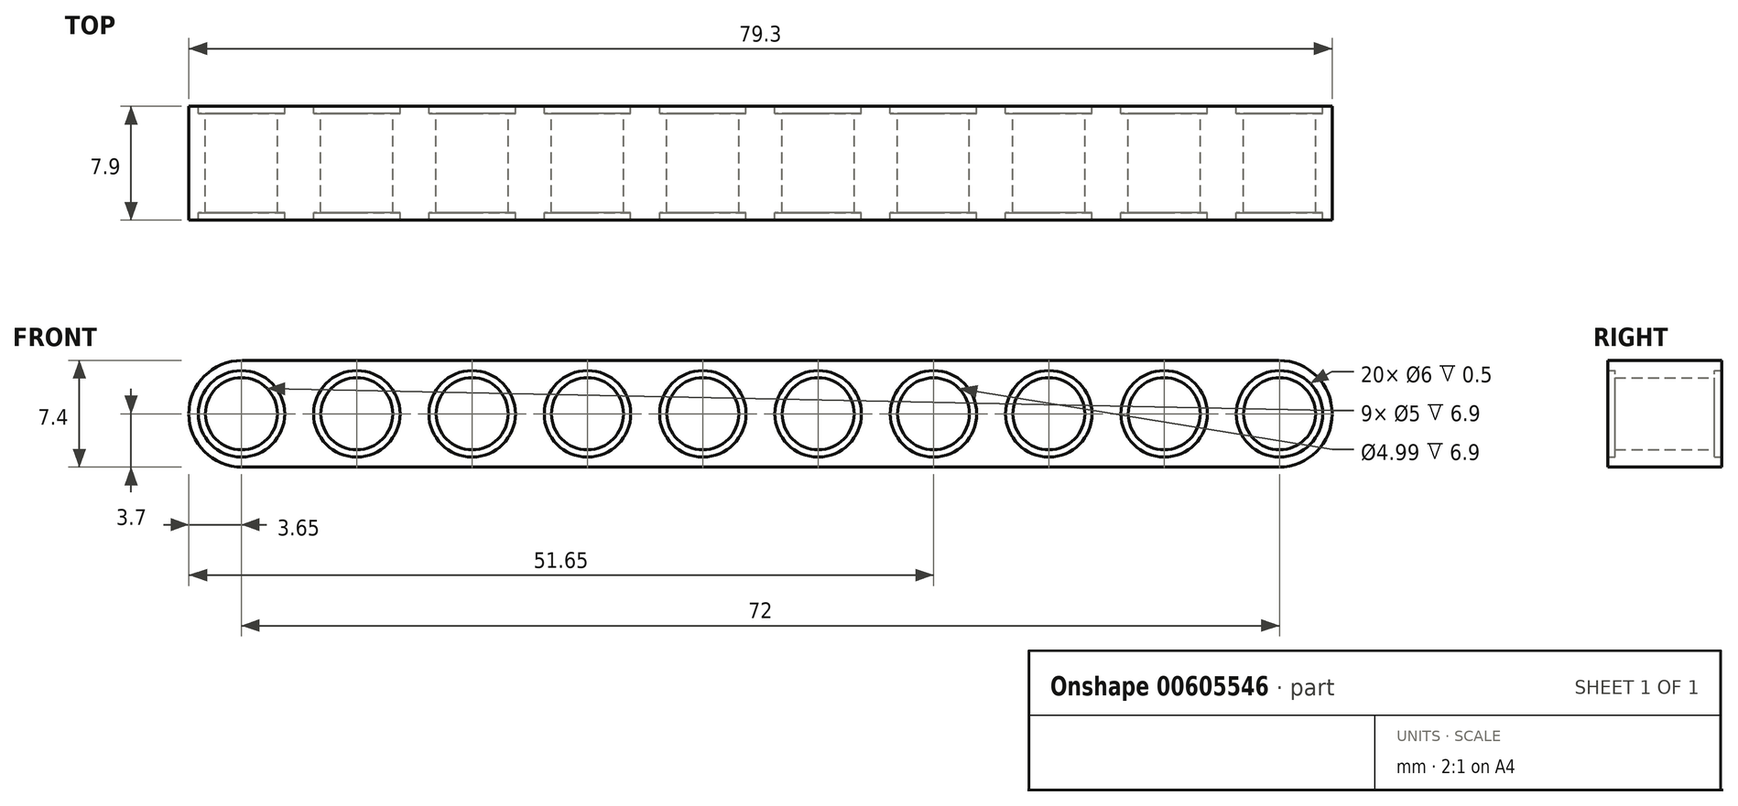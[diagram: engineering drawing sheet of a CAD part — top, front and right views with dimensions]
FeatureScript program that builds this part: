
annotation { "Feature Type Name" : "Feature", "Feature Type Description" : "" }
export const myFeature = defineFeature(function(context is Context, id is Id, definition is map)
    precondition{}
    {
        {
            var Q0;
            Q0=qCreatedBy(makeId("Front.planeOp"),FACE);
            var sketch = newSketch(context, id + "F0", { "sketchPlane" : qUnion([Q0])});
            skLineSegment(sketch, "E0", {"start": v(0, 0) * mm, "end": v(0, 3.7) * mm, "construction": true});
            skLineSegment(sketch, "E1", {"start": v(0, 3.7) * mm, "end": v(0, -3.7) * mm, "construction": true});
            skPoint(sketch, "E1.endSnap0", {"position": v(0, 1.85) * mm});
            skLineSegment(sketch, "E2", {"start": v(-39.65, -3.7) * mm, "end": v(-39.65, 3.7) * mm});
            skLineSegment(sketch, "E3", {"start": v(-39.65, 3.7) * mm, "end": v(39.65, 3.7) * mm});
            skLineSegment(sketch, "E4", {"start": v(39.65, -3.7) * mm, "end": v(39.65, 3.7) * mm});
            skLineSegment(sketch, "E5", {"start": v(-39.65, -3.7) * mm, "end": v(39.65, -3.7) * mm});
            skLineSegment(sketch, "E6", {"start": v(-39.65, 3.7) * mm, "end": v(0, 3.7) * mm});
            skLineSegment(sketch, "E7", {"start": v(0, 0) * mm, "end": v(4, 0) * mm});
            skLineSegment(sketch, "E8", {"start": v(4, 0) * mm, "end": v(-4, 0) * mm});
            skCircle(sketch, "E9", {"center": v(4, 0) * mm, "radius": 3 * mm});
            skCircle(sketch, "E10", {"center": v(-4, 0) * mm, "radius": 3 * mm});
            skLineSegment(sketch, "E11", {"start": v(4, 0) * mm, "end": v(12, 0) * mm, "construction": true});
            skLineSegment(sketch, "E12", {"start": v(12, 0) * mm, "end": v(20, 0) * mm, "construction": true});
            skLineSegment(sketch, "E13", {"start": v(20, 0) * mm, "end": v(28, 0) * mm, "construction": true});
            skLineSegment(sketch, "E14", {"start": v(28, 0) * mm, "end": v(36, 0) * mm, "construction": true});
            skLineSegment(sketch, "E15", {"start": v(-4, 0) * mm, "end": v(-12, 0) * mm, "construction": true});
            skLineSegment(sketch, "E16", {"start": v(-12, 0) * mm, "end": v(-20, 0) * mm, "construction": true});
            skLineSegment(sketch, "E17", {"start": v(-20, 0) * mm, "end": v(-28, 0) * mm, "construction": true});
            skLineSegment(sketch, "E18", {"start": v(-28, 0) * mm, "end": v(-36, 0) * mm, "construction": true});
            skCircle(sketch, "E19", {"center": v(-36, 0) * mm, "radius": 3 * mm});
            skCircle(sketch, "E20", {"center": v(-28, 0) * mm, "radius": 3 * mm});
            skCircle(sketch, "E21", {"center": v(-20, 0) * mm, "radius": 3 * mm});
            skCircle(sketch, "E22", {"center": v(-12, 0) * mm, "radius": 3 * mm});
            skCircle(sketch, "E23", {"center": v(12, 0) * mm, "radius": 3 * mm});
            skCircle(sketch, "E24", {"center": v(20, 0) * mm, "radius": 3 * mm});
            skCircle(sketch, "E25", {"center": v(28, 0) * mm, "radius": 3 * mm});
            skCircle(sketch, "E26", {"center": v(36, 0) * mm, "radius": 3 * mm});
            skCircle(sketch, "E27", {"center": v(-36, 0) * mm, "radius": 2.5 * mm});
            skCircle(sketch, "E28", {"center": v(-28, 0) * mm, "radius": 2.5 * mm});
            skCircle(sketch, "E29", {"center": v(-20, 0) * mm, "radius": 2.5 * mm});
            skCircle(sketch, "E30", {"center": v(-12, 0) * mm, "radius": 2.5 * mm});
            skCircle(sketch, "E31", {"center": v(-4, 0) * mm, "radius": 2.5 * mm});
            skCircle(sketch, "E32", {"center": v(4, 0) * mm, "radius": 2.5 * mm});
            skCircle(sketch, "E33", {"center": v(12, 0) * mm, "radius": 2.5 * mm});
            skCircle(sketch, "E34", {"center": v(20, 0) * mm, "radius": 2.5 * mm});
            skCircle(sketch, "E35", {"center": v(28, 0) * mm, "radius": 2.5 * mm});
            skCircle(sketch, "E36", {"center": v(36, 0) * mm, "radius": 2.5 * mm});
            skSolve(sketch);
        }
        {
            var Q0;
            Q0=makeQuery(id+"F0.imprint","IMPRINT",FACE,{"disambiguationData":[TD([[makeQuery(id+"F0.imprint","IMPRINT",EDGE,{"derivedFrom":sQuery(id+"F0.wireOp",EDGE,"E2")}),-1.0]])]});
            extrude(context, id + "F1", {"entities" : qUnion([Q0]), "endBound" : BoundingType.SYMMETRIC, "depth" : 7.9 * mm, "offsetDistance" : 25 * mm});
        }
        {
            var Q0;
            Q0=makeQuery(id+"F0.imprint","IMPRINT",FACE,{"disambiguationData":[TD([[makeQuery(id+"F0.imprint","IMPRINT",EDGE,{"derivedFrom":sQuery(id+"F0.wireOp",EDGE,"E19")}),1.0]])]});
            var Q1;
            Q1=makeQuery(id+"F0.imprint","IMPRINT",FACE,{"disambiguationData":[TD([[makeQuery(id+"F0.imprint","IMPRINT",EDGE,{"derivedFrom":sQuery(id+"F0.wireOp",EDGE,"E20")}),1.0]])]});
            var Q2;
            Q2=makeQuery(id+"F0.imprint","IMPRINT",FACE,{"disambiguationData":[TD([[makeQuery(id+"F0.imprint","IMPRINT",EDGE,{"derivedFrom":sQuery(id+"F0.wireOp",EDGE,"E21")}),1.0]])]});
            var Q3;
            Q3=makeQuery(id+"F0.imprint","IMPRINT",FACE,{"disambiguationData":[TD([[makeQuery(id+"F0.imprint","IMPRINT",EDGE,{"derivedFrom":sQuery(id+"F0.wireOp",EDGE,"E22")}),1.0]])]});
            var Q4;
            Q4=makeQuery(id+"F0.imprint","IMPRINT",FACE,{"disambiguationData":[TD([[makeQuery(id+"F0.imprint","IMPRINT",EDGE,{"derivedFrom":sQuery(id+"F0.wireOp",EDGE,"E10")}),1.0]])]});
            var Q5;
            Q5=makeQuery(id+"F0.imprint","IMPRINT",FACE,{"disambiguationData":[TD([[makeQuery(id+"F0.imprint","IMPRINT",EDGE,{"derivedFrom":sQuery(id+"F0.wireOp",EDGE,"E9")}),1.0]])]});
            var Q6;
            Q6=makeQuery(id+"F0.imprint","IMPRINT",FACE,{"disambiguationData":[TD([[makeQuery(id+"F0.imprint","IMPRINT",EDGE,{"derivedFrom":sQuery(id+"F0.wireOp",EDGE,"E23")}),1.0]])]});
            var Q7;
            Q7=makeQuery(id+"F0.imprint","IMPRINT",FACE,{"disambiguationData":[TD([[makeQuery(id+"F0.imprint","IMPRINT",EDGE,{"derivedFrom":sQuery(id+"F0.wireOp",EDGE,"E24")}),1.0]])]});
            var Q8;
            Q8=makeQuery(id+"F0.imprint","IMPRINT",FACE,{"disambiguationData":[TD([[makeQuery(id+"F0.imprint","IMPRINT",EDGE,{"derivedFrom":sQuery(id+"F0.wireOp",EDGE,"E25")}),1.0]])]});
            var Q9;
            Q9=makeQuery(id+"F0.imprint","IMPRINT",FACE,{"disambiguationData":[TD([[makeQuery(id+"F0.imprint","IMPRINT",EDGE,{"derivedFrom":sQuery(id+"F0.wireOp",EDGE,"E26")}),1.0]])]});
            extrude(context, id + "F2", {"entities" : qUnion([Q0, Q1, Q2, Q3, Q4, Q5, Q6, Q7, Q8, Q9]), "operationType" : NewBodyOperationType.ADD, "endBound" : BoundingType.SYMMETRIC, "depth" : 6.9 * mm, "offsetDistance" : 25 * mm});
        }
        {
            var Q0;
            Q0=makeQuery(id+"F1.opExtrude","SWEPT_EDGE",EDGE,{"disambiguationData":[OSD([sQuery(id+"F0.wireOp",EDGE,"E3"),sQuery(id+"F0.wireOp",EDGE,"E4")])]});
            var Q1;
            Q1=makeQuery(id+"F1.opExtrude","SWEPT_EDGE",EDGE,{"disambiguationData":[OSD([sQuery(id+"F0.wireOp",EDGE,"E4"),sQuery(id+"F0.wireOp",EDGE,"E5")])]});
            fillet(context, id + "F3", {"entities" : qUnion([Q0, Q1]), "radius" : 3.7 * mm, "tangentPropagation" : true, "allowEdgeOverflow" : false});
        }
        {
            var Q0;
            Q0=makeQuery(id+"F1.opExtrude","SWEPT_EDGE",EDGE,{"disambiguationData":[OSD([sQuery(id+"F0.wireOp",EDGE,"E2"),sQuery(id+"F0.wireOp",EDGE,"E6")])]});
            var Q1;
            Q1=makeQuery(id+"F1.opExtrude","SWEPT_EDGE",EDGE,{"disambiguationData":[OSD([sQuery(id+"F0.wireOp",EDGE,"E2"),sQuery(id+"F0.wireOp",EDGE,"E5")])]});
            fillet(context, id + "F4", {"entities" : qUnion([Q0, Q1]), "radius" : 3.7 * mm, "tangentPropagation" : true, "allowEdgeOverflow" : false});
        }
    });
